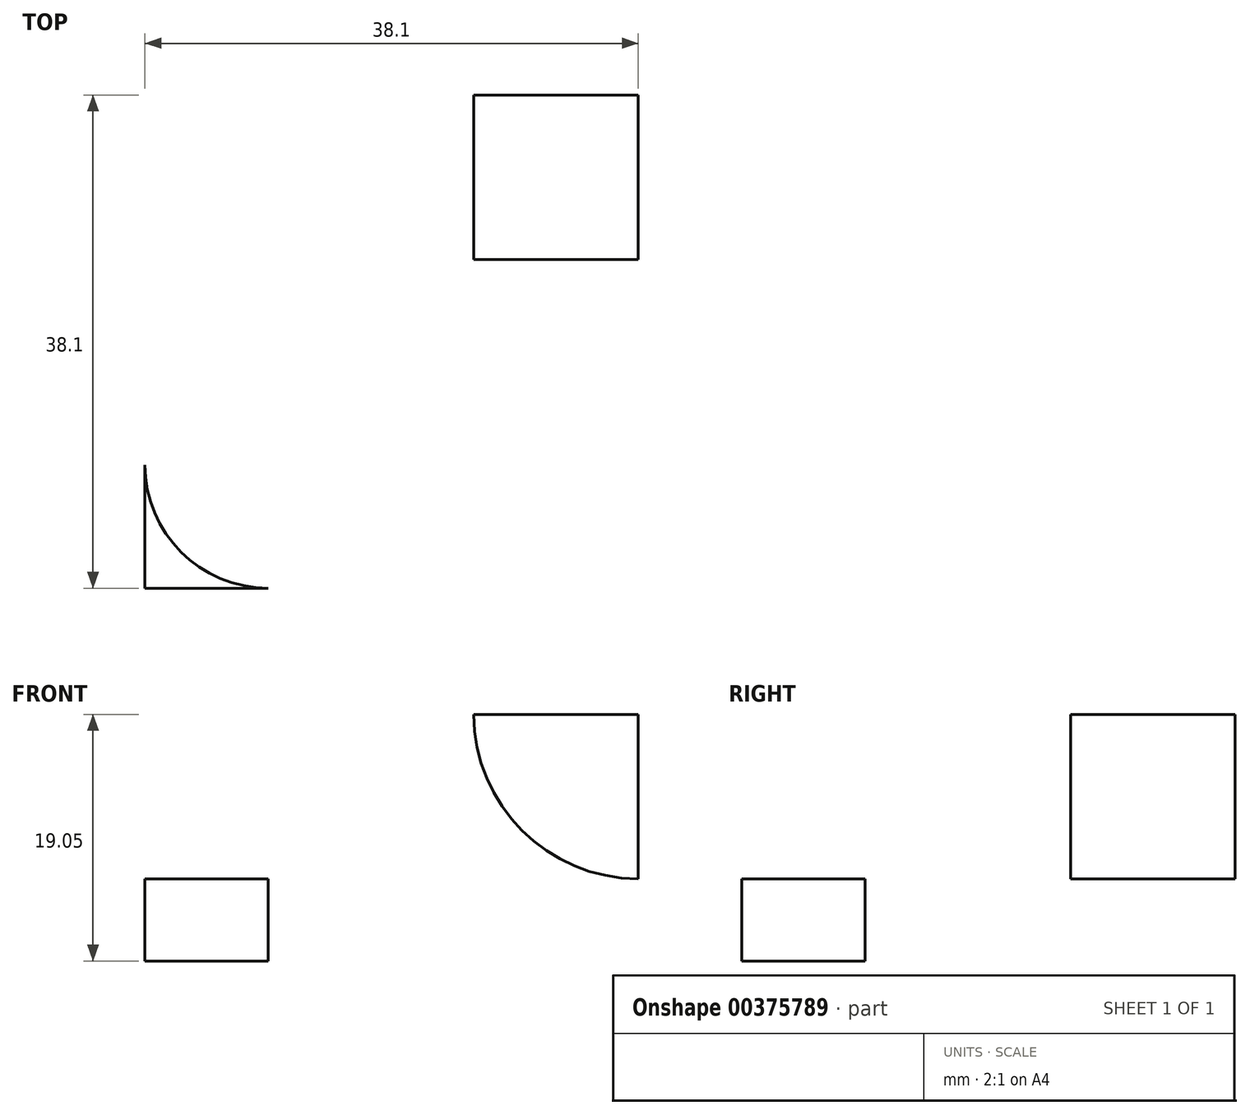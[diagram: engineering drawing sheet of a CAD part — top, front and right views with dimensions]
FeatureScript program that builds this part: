
annotation { "Feature Type Name" : "Feature", "Feature Type Description" : "" }
export const myFeature = defineFeature(function(context is Context, id is Id, definition is map)
    precondition{}
    {
        {
            var Q0;
            Q0=qCreatedBy(makeId("Right.planeOp"),FACE);
            var sketch = newSketch(context, id + "F0", { "sketchPlane" : qUnion([Q0])});
            skLineSegment(sketch, "E0", {"start": v(0, 0) * mm, "end": v(-38.1, 0) * mm});
            skLineSegment(sketch, "E1", {"start": v(-38.1, 0) * mm, "end": v(-38.1, 6.35) * mm});
            skLineSegment(sketch, "E2", {"start": v(-38.1, 6.35) * mm, "end": v(-12.7, 6.35) * mm});
            skLineSegment(sketch, "E3", {"start": v(-12.7, 6.35) * mm, "end": v(-12.7, 44.45) * mm});
            skLineSegment(sketch, "E4", {"start": v(-12.7, 44.45) * mm, "end": v(0, 44.45) * mm});
            skLineSegment(sketch, "E5", {"start": v(0, 44.45) * mm, "end": v(0, 0) * mm});
            skSolve(sketch);
        }
        {
            var Q0;
            Q0=makeQuery(id+"F0.imprint","IMPRINT",FACE,{"disambiguationData":[TD([[makeQuery(id+"F0.imprint","IMPRINT",EDGE,{"derivedFrom":sQuery(id+"F0.wireOp",EDGE,"E0")}),-1.0]])]});
            extrude(context, id + "F1", {"entities" : qUnion([Q0]), "depth" : 63.5 * mm});
        }
        {
            var Q0;
            Q0=makeQuery(id+"F1.opExtrude","SWEPT_FACE",FACE,{"disambiguationData":[OSD([sQuery(id+"F0.wireOp",EDGE,"E3")])]});
            var sketch = newSketch(context, id + "F2", { "sketchPlane" : qUnion([Q0])});
            skLineSegment(sketch, "E6", {"start": v(38.1, 44.45) * mm, "end": v(38.1, 6.35) * mm});
            skSolve(sketch);
        }
        {
            var Q0;
            {var subQ0=sQuery(id+"F2.wireOp",EDGE,"E6");Q0=makeQuery(id+"F2.imprint","IMPRINT",FACE,{"disambiguationData":[TD([[makeQuery(id+"F2.imprint","IMPRINT",EDGE,{"derivedFrom":subQ0}),1.0]])]});}
            extrude(context, id + "F3", {"entities" : qUnion([Q0]), "operationType" : NewBodyOperationType.REMOVE, "oppositeDirection" : true, "depth" : 25.4 * mm});
        }
        {
            var Q0;
            Q0=makeQuery(id+"F1.opExtrude","SWEPT_FACE",FACE,{"disambiguationData":[OSD([sQuery(id+"F0.wireOp",EDGE,"E3")])]});
            var sketch = newSketch(context, id + "F4", { "sketchPlane" : qUnion([Q0])});
            skLineSegment(sketch, "E7", {"start": v(25.4, 44.45) * mm, "end": v(25.4, 31.75) * mm});
            skLineSegment(sketch, "E8", {"start": v(25.4, 31.75) * mm, "end": v(38.1, 31.75) * mm});
            skSolve(sketch);
        }
        {
            var Q0;
            {var subQ0=sQuery(id+"F4.wireOp",EDGE,"E7");Q0=makeQuery(id+"F4.imprint","IMPRINT",FACE,{"disambiguationData":[TD([[makeQuery(id+"F4.imprint","IMPRINT",EDGE,{"derivedFrom":subQ0}),1.0]])]});}
            extrude(context, id + "F5", {"entities" : qUnion([Q0]), "operationType" : NewBodyOperationType.REMOVE, "oppositeDirection" : true, "depth" : 25.4 * mm});
        }
        {
            var Q0;
            Q0=makeQuery(id+"F1.opExtrude","SWEPT_FACE",FACE,{"disambiguationData":[OSD([sQuery(id+"F0.wireOp",EDGE,"E3")])]});
            var sketch = newSketch(context, id + "F6", { "sketchPlane" : qUnion([Q0])});
            skCircle(sketch, "E9", {"center": v(12.7, 31.75) * mm, "radius": 6.35 * mm});
            skPoint(sketch, "E9.centerSnap0", {"position": v(12.7, 44.45) * mm});
            skArc(sketch, "E10", {"start": v(25.4, 31.75) * mm, "mid": v(12.7, 44.45) * mm, "end": v(0, 31.75) * mm});
            skSolve(sketch);
        }
        {
            var Q0;
            Q0=makeQuery(id+"F6.imprint","IMPRINT",FACE,{"disambiguationData":[TD([[makeQuery(id+"F6.imprint","IMPRINT",EDGE,{"derivedFrom":sQuery(id+"F6.wireOp",EDGE,"E9")}),1.0]])]});
            var Q1;
            {var subQ0=sQuery(id+"F6.wireOp",EDGE,"E10");var subQ1=sQuery(id+"F0.wireOp",EDGE,"E3");var subQ2=makeQuery(id+"F1.opExtrude","CAP_EDGE",EDGE,{"disambiguationData":[OSD([subQ1])],"isStart":true});var subQ3=makeQuery(id+"F6.imprint","INTERSECT",VERTEX,{"derivedFrom":[subQ2,subQ0]});Q1=makeQuery(id+"F6.imprint","IMPRINT",FACE,{"disambiguationData":[TD([[makeQuery(id+"F6.imprint","IMPRINT",EDGE,{"disambiguationData":[TD([[subQ3,1.0]])],"derivedFrom":subQ0}),-1.0]])]});}
            var Q2;
            {var subQ1=makeQuery(id+"F5.boolean.opBoolean","COPY",EDGE,{"derivedFrom":makeQuery(id+"F5.opExtrude","CAP_EDGE",EDGE,{"disambiguationData":[OSD([sQuery(id+"F4.wireOp",EDGE,"E7")])],"isStart":true})});Q2=makeQuery(id+"F6.imprint","IMPRINT",FACE,{"disambiguationData":[TD([[makeQuery(id+"F6.imprint","IMPRINT",EDGE,{"derivedFrom":subQ1}),-1.0]])]});}
            extrude(context, id + "F7", {"entities" : qUnion([Q0, Q1, Q2]), "operationType" : NewBodyOperationType.REMOVE, "oppositeDirection" : true, "depth" : 25.4 * mm});
        }
        {
            var Q0;
            Q0=makeQuery(id+"F1.opExtrude","SWEPT_FACE",FACE,{"disambiguationData":[OSD([sQuery(id+"F0.wireOp",EDGE,"E3")])]});
            var sketch = newSketch(context, id + "F8", { "sketchPlane" : qUnion([Q0])});
            skLineSegment(sketch, "E11", {"start": v(25.4, 31.75) * mm, "end": v(25.4, 19.05) * mm});
            skLineSegment(sketch, "E12", {"start": v(25.4, 19.05) * mm, "end": v(38.1, 19.05) * mm});
            skSolve(sketch);
        }
        {
            var Q0;
            Q0=makeQuery(id+"F8.imprint","IMPRINT",FACE,{"disambiguationData":[TD([[makeQuery(id+"F8.imprint","IMPRINT",EDGE,{"derivedFrom":sQuery(id+"F8.wireOp",EDGE,"E11")}),1.0]])]});
            extrude(context, id + "F9", {"entities" : qUnion([Q0]), "operationType" : NewBodyOperationType.REMOVE, "oppositeDirection" : true, "depth" : 25.4 * mm});
        }
        {
            var Q0;
            Q0=makeQuery(id+"F1.opExtrude","SWEPT_FACE",FACE,{"disambiguationData":[OSD([sQuery(id+"F0.wireOp",EDGE,"E3")])]});
            var sketch = newSketch(context, id + "F10", { "sketchPlane" : qUnion([Q0])});
            skArc(sketch, "E13", {"start": v(38.1, 6.35) * mm, "mid": v(29.12, 10.07) * mm, "end": v(25.4, 19.05) * mm});
            skSolve(sketch);
        }
        {
            var Q0;
            Q0=makeQuery(id+"F10.imprint","IMPRINT",FACE,{"disambiguationData":[TD([[makeQuery(id+"F10.imprint","IMPRINT",EDGE,{"derivedFrom":sQuery(id+"F10.wireOp",EDGE,"E13")}),-1.0]])]});
            extrude(context, id + "F11", {"entities" : qUnion([Q0]), "operationType" : NewBodyOperationType.REMOVE, "oppositeDirection" : true, "depth" : 25.4 * mm});
        }
        {
            var Q0;
            {var subQ0=sQuery(id+"F0.wireOp",EDGE,"E2");Q0=makeQuery(id+"F3.boolean.opBoolean","MERGE",FACE,{"derivedFrom":[makeQuery(id+"F1.opExtrude","SWEPT_FACE",FACE,{"disambiguationData":[OSD([subQ0])]}),makeQuery(id+"F3.opExtrude","SWEPT_FACE",FACE,{"disambiguationData":[OSD([subQ0,sQuery(id+"F0.wireOp",EDGE,"E3")])]})]});}
            var sketch = newSketch(context, id + "F12", { "sketchPlane" : qUnion([Q0])});
            skCircle(sketch, "E14", {"center": v(9.53, -28.57) * mm, "radius": 3.18 * mm});
            skCircle(sketch, "E15", {"center": v(53.98, -28.57) * mm, "radius": 3.18 * mm});
            skCircle(sketch, "E16", {"center": v(53.98, -9.52) * mm, "radius": 3.18 * mm});
            skArc(sketch, "E17", {"start": v(9.52, -38.1) * mm, "mid": v(2.79, -35.31) * mm, "end": v(0, -28.57) * mm});
            skArc(sketch, "E18", {"start": v(53.98, -38.1) * mm, "mid": v(60.71, -35.31) * mm, "end": v(63.5, -28.57) * mm});
            skSolve(sketch);
        }
        {
            var Q0;
            Q0=makeQuery(id+"F12.imprint","IMPRINT",FACE,{"disambiguationData":[TD([[makeQuery(id+"F12.imprint","IMPRINT",EDGE,{"derivedFrom":sQuery(id+"F12.wireOp",EDGE,"E16")}),1.0]])]});
            var Q1;
            Q1=makeQuery(id+"F12.imprint","IMPRINT",FACE,{"disambiguationData":[TD([[makeQuery(id+"F12.imprint","IMPRINT",EDGE,{"derivedFrom":sQuery(id+"F12.wireOp",EDGE,"E15")}),1.0]])]});
            var Q2;
            Q2=makeQuery(id+"F12.imprint","IMPRINT",FACE,{"disambiguationData":[TD([[makeQuery(id+"F12.imprint","IMPRINT",EDGE,{"derivedFrom":sQuery(id+"F12.wireOp",EDGE,"E14")}),1.0]])]});
            var Q3;
            {var subQ0=sQuery(id+"F12.wireOp",EDGE,"E17");Q3=makeQuery(id+"F12.imprint","IMPRINT",FACE,{"disambiguationData":[TD([[makeQuery(id+"F12.imprint","IMPRINT",EDGE,{"derivedFrom":subQ0}),1.0]])]});}
            var Q4;
            {var subQ0=sQuery(id+"F12.wireOp",EDGE,"E18");Q4=makeQuery(id+"F12.imprint","IMPRINT",FACE,{"disambiguationData":[TD([[makeQuery(id+"F12.imprint","IMPRINT",EDGE,{"derivedFrom":subQ0}),-1.0]])]});}
            extrude(context, id + "F13", {"entities" : qUnion([Q0, Q1, Q2, Q3, Q4]), "operationType" : NewBodyOperationType.REMOVE, "oppositeDirection" : true, "depth" : 25.4 * mm});
        }
    });
